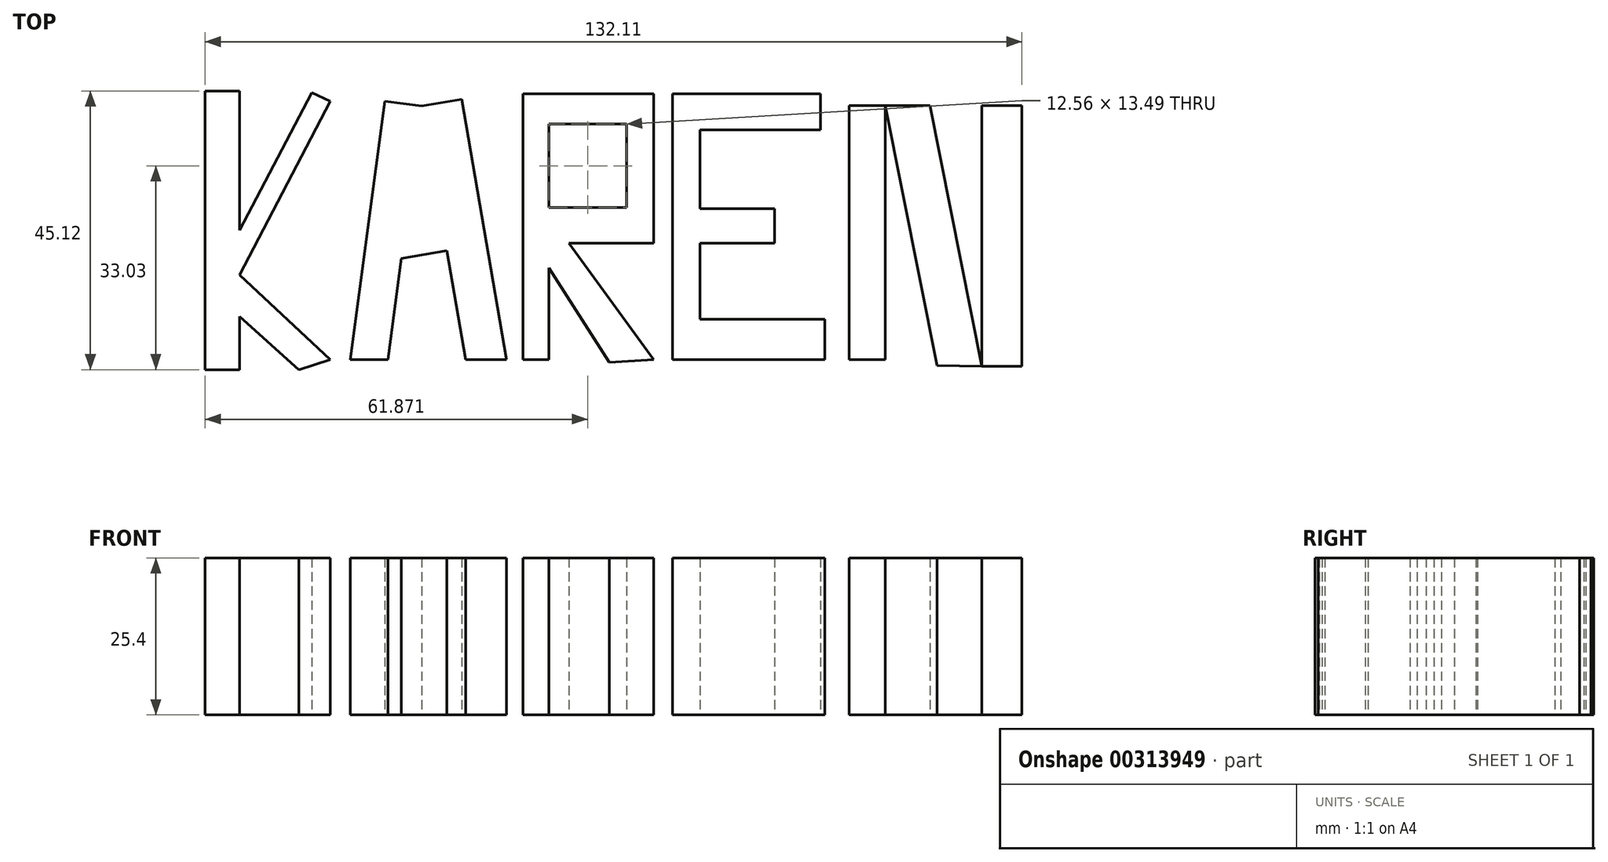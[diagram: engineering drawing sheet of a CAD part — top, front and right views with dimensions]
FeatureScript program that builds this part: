
annotation { "Feature Type Name" : "Feature", "Feature Type Description" : "" }
export const myFeature = defineFeature(function(context is Context, id is Id, definition is map)
    precondition{}
    {
        {
            var Q0;
            Q0=qCreatedBy(makeId("Top.planeOp"),FACE);
            var sketch = newSketch(context, id + "F0", { "sketchPlane" : qUnion([Q0])});
            skLineSegment(sketch, "E0.bottom", {"start": v(-72.57, 24.65) * mm, "end": v(-66.99, 24.65) * mm});
            skLineSegment(sketch, "E0.top", {"start": v(-72.57, -20.47) * mm, "end": v(-66.99, -20.47) * mm});
            skLineSegment(sketch, "E0.left", {"start": v(-72.57, 24.65) * mm, "end": v(-72.57, -20.47) * mm});
            skLineSegment(sketch, "E0.right", {"start": v(-66.99, 24.65) * mm, "end": v(-66.99, -20.47) * mm});
            skLineSegment(sketch, "E1", {"start": v(-66.99, 2.1) * mm, "end": v(-55.36, 24.42) * mm});
            skLineSegment(sketch, "E2", {"start": v(-66.99, -5.12) * mm, "end": v(-52.33, 23.02) * mm});
            skLineSegment(sketch, "E3", {"start": v(-55.36, 24.42) * mm, "end": v(-52.33, 23.02) * mm});
            skLineSegment(sketch, "E4", {"start": v(-66.99, -5.12) * mm, "end": v(-52.33, -18.84) * mm});
            skLineSegment(sketch, "E5", {"start": v(-66.99, -11.86) * mm, "end": v(-57.45, -20.47) * mm});
            skLineSegment(sketch, "E6", {"start": v(-57.45, -20.47) * mm, "end": v(-52.33, -18.84) * mm});
            skLineSegment(sketch, "E7", {"start": v(-49.08, -18.84) * mm, "end": v(-43.5, 23.02) * mm});
            skLineSegment(sketch, "E8", {"start": v(-43.5, 23.02) * mm, "end": v(-37.55, 22.23) * mm});
            skLineSegment(sketch, "E9", {"start": v(-37.55, 22.23) * mm, "end": v(-43.03, -18.84) * mm});
            skLineSegment(sketch, "E10", {"start": v(-49.08, -18.84) * mm, "end": v(-43.03, -18.84) * mm});
            skLineSegment(sketch, "E11", {"start": v(-37.55, 22.23) * mm, "end": v(-30.47, -18.84) * mm});
            skLineSegment(sketch, "E12", {"start": v(-37.55, 22.23) * mm, "end": v(-31.1, 23.35) * mm});
            skLineSegment(sketch, "E13", {"start": v(-31.1, 23.35) * mm, "end": v(-23.82, -18.84) * mm});
            skLineSegment(sketch, "E14", {"start": v(-30.47, -18.84) * mm, "end": v(-23.82, -18.84) * mm});
            skLineSegment(sketch, "E15", {"start": v(-40.3, 1.7) * mm, "end": v(-34.2, 2.75) * mm});
            skLineSegment(sketch, "E16", {"start": v(-40.85, -2.48) * mm, "end": v(-33.5, -1.21) * mm});
            skLineSegment(sketch, "E17.bottom", {"start": v(-21.17, -18.84) * mm, "end": v(-16.98, -18.84) * mm});
            skLineSegment(sketch, "E17.top", {"start": v(-21.17, 24.19) * mm, "end": v(-16.98, 24.19) * mm});
            skLineSegment(sketch, "E17.left", {"start": v(-21.17, -18.84) * mm, "end": v(-21.17, 24.19) * mm});
            skLineSegment(sketch, "E17.right", {"start": v(-16.98, -18.84) * mm, "end": v(-16.98, 24.19) * mm});
            skLineSegment(sketch, "E18.bottom", {"start": v(-16.98, 24.19) * mm, "end": v(0, 24.19) * mm});
            skLineSegment(sketch, "E18.top", {"start": v(-16.98, 19.3) * mm, "end": v(0, 19.3) * mm});
            skLineSegment(sketch, "E18.left", {"start": v(-16.98, 24.19) * mm, "end": v(-16.98, 19.3) * mm});
            skLineSegment(sketch, "E18.right", {"start": v(0, 24.19) * mm, "end": v(0, 19.3) * mm});
            skLineSegment(sketch, "E19.bottom", {"start": v(-4.42, 19.3) * mm, "end": v(0, 19.3) * mm});
            skLineSegment(sketch, "E19.top", {"start": v(-4.42, 5.81) * mm, "end": v(0, 5.81) * mm});
            skLineSegment(sketch, "E19.left", {"start": v(-4.42, 19.3) * mm, "end": v(-4.42, 5.81) * mm});
            skLineSegment(sketch, "E19.right", {"start": v(0, 19.3) * mm, "end": v(0, 5.81) * mm});
            skLineSegment(sketch, "E20.bottom", {"start": v(0, 5.81) * mm, "end": v(-16.98, 5.81) * mm});
            skLineSegment(sketch, "E20.top", {"start": v(0, 0) * mm, "end": v(-16.98, 0) * mm});
            skLineSegment(sketch, "E20.left", {"start": v(0, 5.81) * mm, "end": v(0, 0) * mm});
            skLineSegment(sketch, "E20.right", {"start": v(-16.98, 5.81) * mm, "end": v(-16.98, 0) * mm});
            skLineSegment(sketch, "E21", {"start": v(-16.98, -3.95) * mm, "end": v(-7.21, -19.3) * mm});
            skLineSegment(sketch, "E22", {"start": v(-13.72, 0) * mm, "end": v(0, -18.84) * mm});
            skLineSegment(sketch, "E23", {"start": v(-7.21, -19.3) * mm, "end": v(0, -18.84) * mm});
            skLineSegment(sketch, "E24.bottom", {"start": v(3.02, 24.19) * mm, "end": v(7.44, 24.19) * mm});
            skLineSegment(sketch, "E24.top", {"start": v(3.02, -18.84) * mm, "end": v(7.44, -18.84) * mm});
            skLineSegment(sketch, "E24.left", {"start": v(3.02, 24.19) * mm, "end": v(3.02, -18.84) * mm});
            skLineSegment(sketch, "E24.right", {"start": v(7.44, 24.19) * mm, "end": v(7.44, -18.84) * mm});
            skLineSegment(sketch, "E25.bottom", {"start": v(7.44, 24.19) * mm, "end": v(26.98, 24.19) * mm});
            skLineSegment(sketch, "E25.top", {"start": v(7.44, 18.37) * mm, "end": v(26.98, 18.37) * mm});
            skLineSegment(sketch, "E25.left", {"start": v(7.44, 24.19) * mm, "end": v(7.44, 18.37) * mm});
            skLineSegment(sketch, "E25.right", {"start": v(26.98, 24.19) * mm, "end": v(26.98, 18.37) * mm});
            skLineSegment(sketch, "E26.bottom", {"start": v(7.44, -18.84) * mm, "end": v(27.68, -18.84) * mm});
            skLineSegment(sketch, "E26.top", {"start": v(7.44, -12.33) * mm, "end": v(27.68, -12.33) * mm});
            skLineSegment(sketch, "E26.left", {"start": v(7.44, -18.84) * mm, "end": v(7.44, -12.33) * mm});
            skLineSegment(sketch, "E26.right", {"start": v(27.68, -18.84) * mm, "end": v(27.68, -12.33) * mm});
            skLineSegment(sketch, "E27.bottom", {"start": v(7.44, 5.58) * mm, "end": v(19.54, 5.58) * mm});
            skLineSegment(sketch, "E27.top", {"start": v(7.44, 0) * mm, "end": v(19.54, 0) * mm});
            skLineSegment(sketch, "E27.left", {"start": v(7.44, 5.58) * mm, "end": v(7.44, 0) * mm});
            skLineSegment(sketch, "E27.right", {"start": v(19.54, 5.58) * mm, "end": v(19.54, 0) * mm});
            skLineSegment(sketch, "E28.bottom", {"start": v(31.63, 22.33) * mm, "end": v(37.45, 22.33) * mm});
            skLineSegment(sketch, "E28.top", {"start": v(31.63, -18.84) * mm, "end": v(37.45, -18.84) * mm});
            skLineSegment(sketch, "E28.left", {"start": v(31.63, 22.33) * mm, "end": v(31.63, -18.84) * mm});
            skLineSegment(sketch, "E28.right", {"start": v(37.45, 22.33) * mm, "end": v(37.45, -18.84) * mm});
            skLineSegment(sketch, "E29", {"start": v(37.45, 22.33) * mm, "end": v(45.82, -19.77) * mm});
            skLineSegment(sketch, "E30", {"start": v(37.45, 22.33) * mm, "end": v(44.66, 22.33) * mm});
            skLineSegment(sketch, "E31", {"start": v(44.66, 22.33) * mm, "end": v(53.07, -19.95) * mm});
            skLineSegment(sketch, "E32", {"start": v(45.82, -19.77) * mm, "end": v(53.07, -19.95) * mm});
            skLineSegment(sketch, "E33", {"start": v(53.07, -19.95) * mm, "end": v(53.07, 22.33) * mm});
            skLineSegment(sketch, "E34", {"start": v(53.07, 22.33) * mm, "end": v(59.54, 22.33) * mm});
            skLineSegment(sketch, "E35", {"start": v(59.54, 22.33) * mm, "end": v(59.54, -19.95) * mm});
            skLineSegment(sketch, "E36", {"start": v(53.07, -19.95) * mm, "end": v(59.54, -19.95) * mm});
            skSolve(sketch);
        }
        {
            var Q0;
            Q0 = qSketchRegion(id + "F0", true);
            extrude(context, id + "F1", {"entities" : qUnion([Q0]), "depth" : 25.4 * mm});
        }
    });
